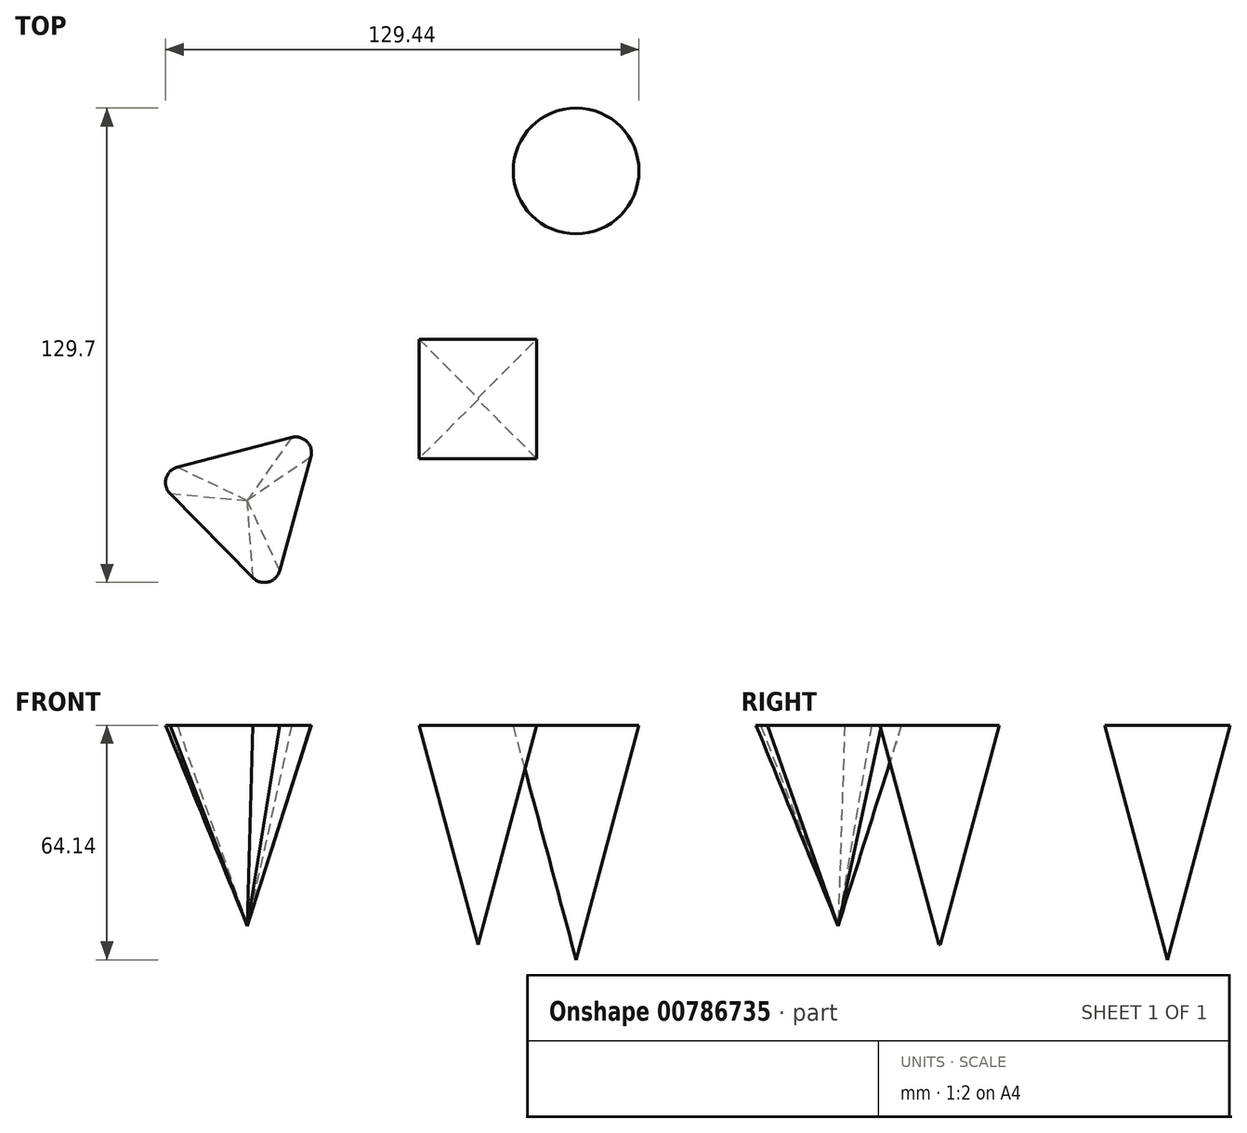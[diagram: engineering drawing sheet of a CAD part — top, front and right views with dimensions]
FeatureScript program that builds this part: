
annotation { "Feature Type Name" : "Feature", "Feature Type Description" : "" }
export const myFeature = defineFeature(function(context is Context, id is Id, definition is map)
    precondition{}
    {
        {
            var Q0;
            Q0=qCreatedBy(makeId("Top.planeOp"),FACE);
            var sketch = newSketch(context, id + "F0", { "sketchPlane" : qUnion([Q0])});
            skLineSegment(sketch, "E0.bottom", {"start": v(0, 0) * mm, "end": v(32.17, 0) * mm});
            skLineSegment(sketch, "E0.top", {"start": v(0, -32.64) * mm, "end": v(32.17, -32.64) * mm});
            skLineSegment(sketch, "E0.left", {"start": v(0, 0) * mm, "end": v(0, -32.64) * mm});
            skLineSegment(sketch, "E0.right", {"start": v(32.17, 0) * mm, "end": v(32.17, -32.64) * mm});
            skSolve(sketch);
        }
        {
            var Q0;
            Q0=makeQuery(id+"F0.imprint","IMPRINT",FACE,{"disambiguationData":[TD([[makeQuery(id+"F0.imprint","IMPRINT",EDGE,{"derivedFrom":sQuery(id+"F0.wireOp",EDGE,"E0.bottom")}),-1.0]])]});
            extrude(context, id + "F1", {"entities" : qUnion([Q0]), "oppositeDirection" : true, "depth" : 67.3 * mm, "offsetDistance" : 25.4 * mm, "hasDraft" : true, "draftAngle" : 15 * degree, "draftPullDirection" : true});
        }
        {
            var Q0;
            Q0=qCreatedBy(makeId("Top.planeOp"),FACE);
            var sketch = newSketch(context, id + "F2", { "sketchPlane" : qUnion([Q0])});
            skCircle(sketch, "E1", {"center": v(42.94, 46) * mm, "radius": 17.19 * mm});
            skSolve(sketch);
        }
        {
            var Q0;
            Q0=makeQuery(id+"F2.imprint","IMPRINT",FACE,{"disambiguationData":[TD([[makeQuery(id+"F2.imprint","IMPRINT",EDGE,{"derivedFrom":sQuery(id+"F2.wireOp",EDGE,"E1")}),1.0]])]});
            extrude(context, id + "F3", {"entities" : qUnion([Q0]), "oppositeDirection" : true, "depth" : 79.25 * mm, "offsetDistance" : 25.4 * mm, "hasDraft" : true, "draftAngle" : 15 * degree, "draftPullDirection" : true});
        }
        {
            var Q0;
            Q0=qCreatedBy(makeId("Top.planeOp"),FACE);
            var sketch = newSketch(context, id + "F4", { "sketchPlane" : qUnion([Q0])});
            skCircle(sketch, "E2.cCircle", {"center": v(-47, -44.13) * mm, "radius": 13.67 * mm, "construction": true});
            skLineSegment(sketch, "E2.0", {"start": v(-66.07, -34.97) * mm, "end": v(-34.84, -26.83) * mm});
            skLineSegment(sketch, "E2.1", {"start": v(-29.55, -32.2) * mm, "end": v(-38.11, -63.3) * mm});
            skLineSegment(sketch, "E2.2", {"start": v(-45.4, -65.21) * mm, "end": v(-68.07, -42.24) * mm});
            skPoint(sketch, "E2.0.midPoint", {"position": v(-50.46, -30.9) * mm});
            skPoint(sketch, "E3.visualSharp", {"position": v(-40.11, -70.57) * mm});
            skArc(sketch, "E3.filletArc", {"start": v(-45.4, -65.21) * mm, "mid": v(-41.21, -66.36) * mm, "end": v(-38.11, -63.3) * mm});
            skPoint(sketch, "E4.visualSharp", {"position": v(-27.55, -24.93) * mm});
            skArc(sketch, "E4.filletArc", {"start": v(-29.55, -32.2) * mm, "mid": v(-30.65, -27.99) * mm, "end": v(-34.84, -26.83) * mm});
            skPoint(sketch, "E5.visualSharp", {"position": v(-73.36, -36.87) * mm});
            skArc(sketch, "E5.filletArc", {"start": v(-66.07, -34.97) * mm, "mid": v(-69.16, -38.03) * mm, "end": v(-68.07, -42.24) * mm});
            skSolve(sketch);
        }
        {
            var Q0;
            Q0=qCreatedBy(makeId("Top.planeOp"),FACE);
            cPlane(context, id + "F5", {"entities" : qUnion([Q0]), "cplaneType" : CPlaneType.OFFSET, "offset" : 54.86 * mm, "oppositeDirection" : true, "width" : 152.4 * mm, "height" : 152.4 * mm});
        }
        {
            var Q0;
            Q0=qCreatedBy(id+"F5.planeOp",FACE);
            var sketch = newSketch(context, id + "F6", { "sketchPlane" : qUnion([Q0])});
            skCircle(sketch, "E6", {"center": v(-46.94, -44.07) * mm, "radius": 0.55 * mm});
            skSolve(sketch);
        }
        {
            var Q0;
            Q0=makeQuery(id+"F4.imprint","IMPRINT",FACE,{"disambiguationData":[TD([[makeQuery(id+"F4.imprint","IMPRINT",EDGE,{"derivedFrom":sQuery(id+"F4.wireOp",EDGE,"E2.0")}),-1.0]])]});
            var Q1;
            Q1=sQuery(id+"F6.wireOp",VERTEX,"E6.center");
            loft(context, id + "F7", {"sheetProfilesArray" : [{ "sheetProfileEntities" : qUnion([Q0]) }, { "sheetProfileEntities" : qUnion([Q1]) }]});
        }
    });
